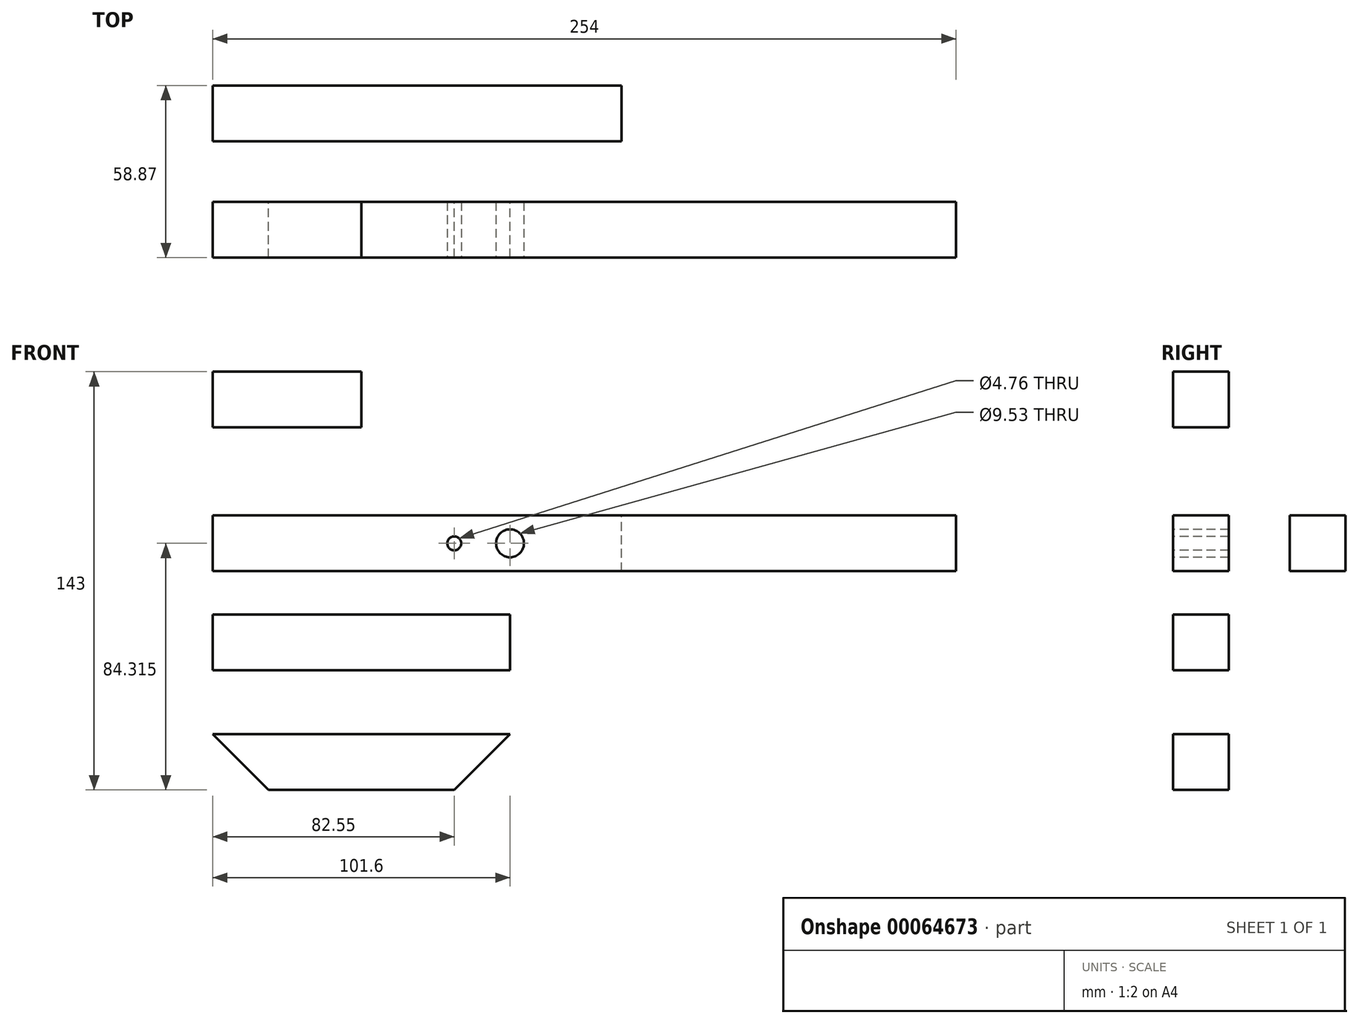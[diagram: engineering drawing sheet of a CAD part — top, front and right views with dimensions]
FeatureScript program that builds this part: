
annotation { "Feature Type Name" : "Feature", "Feature Type Description" : "" }
export const myFeature = defineFeature(function(context is Context, id is Id, definition is map)
    precondition{}
    {
        {
            var Q0;
            Q0=qCreatedBy(makeId("Front.planeOp"),FACE);
            var sketch = newSketch(context, id + "F0", { "sketchPlane" : qUnion([Q0])});
            skLineSegment(sketch, "E0.bottom", {"start": v(0, 0) * mm, "end": v(254, 0) * mm});
            skLineSegment(sketch, "E0.top", {"start": v(0, 19.05) * mm, "end": v(254, 19.05) * mm});
            skLineSegment(sketch, "E0.left", {"start": v(0, 0) * mm, "end": v(0, 19.05) * mm});
            skLineSegment(sketch, "E0.right", {"start": v(254, 0) * mm, "end": v(254, 19.05) * mm});
            skSolve(sketch);
        }
        {
            var Q0;
            Q0 = qSketchRegion(id + "F0", true);
            extrude(context, id + "F1", {"entities" : qUnion([Q0]), "depth" : 19.05 * mm});
        }
        {
            var Q0;
            Q0=makeQuery(id+"F1.opExtrude","CAP_FACE",FACE,{"disambiguationData":[OSD([sQuery(id+"F0.wireOp",EDGE,"E0.bottom"),sQuery(id+"F0.wireOp",EDGE,"E0.top"),sQuery(id+"F0.wireOp",EDGE,"E0.left"),sQuery(id+"F0.wireOp",EDGE,"E0.right")])],"isStart":false});
            var sketch = newSketch(context, id + "F2", { "sketchPlane" : qUnion([Q0])});
            skLineSegment(sketch, "E1", {"start": v(0, 9.53) * mm, "end": v(82.55, 9.53) * mm});
            skLineSegment(sketch, "E2", {"start": v(82.55, 9.53) * mm, "end": v(101.6, 9.53) * mm});
            skPoint(sketch, "E2.endSnap0", {"position": v(127, 19.05) * mm});
            skCircle(sketch, "E3", {"center": v(82.55, 9.53) * mm, "radius": 2.38 * mm});
            skCircle(sketch, "E4", {"center": v(101.6, 9.53) * mm, "radius": 4.76 * mm});
            skSolve(sketch);
        }
        {
            var Q0;
            Q0 = qSketchRegion(id + "F2", true);
            extrude(context, id + "F3", {"entities" : qUnion([Q0]), "operationType" : NewBodyOperationType.REMOVE, "oppositeDirection" : true, "depth" : 25.4 * mm});
        }
        {
            var Q0;
            Q0=qCreatedBy(makeId("Front.planeOp"),FACE);
            var sketch = newSketch(context, id + "F4", { "sketchPlane" : qUnion([Q0])});
            skLineSegment(sketch, "E5.bottom", {"start": v(0, -14.84) * mm, "end": v(101.6, -14.84) * mm});
            skLineSegment(sketch, "E5.top", {"start": v(0, -33.89) * mm, "end": v(101.6, -33.89) * mm});
            skLineSegment(sketch, "E5.left", {"start": v(0, -14.84) * mm, "end": v(0, -33.89) * mm});
            skLineSegment(sketch, "E5.right", {"start": v(101.6, -14.84) * mm, "end": v(101.6, -33.89) * mm});
            skSolve(sketch);
        }
        {
            var Q0;
            Q0 = qSketchRegion(id + "F4", true);
            extrude(context, id + "F5", {"entities" : qUnion([Q0]), "depth" : 19.05 * mm});
        }
        {
            var Q0;
            Q0=qCreatedBy(makeId("Front.planeOp"),FACE);
            var sketch = newSketch(context, id + "F6", { "sketchPlane" : qUnion([Q0])});
            skLineSegment(sketch, "E6.bottom", {"start": v(0, -55.74) * mm, "end": v(101.6, -55.74) * mm});
            skLineSegment(sketch, "E6.top", {"start": v(19.05, -74.8) * mm, "end": v(82.55, -74.8) * mm});
            skLineSegment(sketch, "E7", {"start": v(0, -55.74) * mm, "end": v(19.05, -74.8) * mm});
            skLineSegment(sketch, "E8", {"start": v(101.6, -55.74) * mm, "end": v(82.55, -74.8) * mm});
            skSolve(sketch);
        }
        {
            var Q0;
            Q0 = qSketchRegion(id + "F6", true);
            extrude(context, id + "F7", {"entities" : qUnion([Q0]), "depth" : 19.05 * mm});
        }
        {
            var Q0;
            Q0=qCreatedBy(makeId("Front.planeOp"),FACE);
            var sketch = newSketch(context, id + "F8", { "sketchPlane" : qUnion([Q0])});
            skLineSegment(sketch, "E9.bottom", {"start": v(0, 68.2) * mm, "end": v(50.8, 68.2) * mm});
            skLineSegment(sketch, "E9.top", {"start": v(0, 49.16) * mm, "end": v(50.8, 49.16) * mm});
            skLineSegment(sketch, "E9.left", {"start": v(0, 68.2) * mm, "end": v(0, 49.16) * mm});
            skLineSegment(sketch, "E9.right", {"start": v(50.8, 68.2) * mm, "end": v(50.8, 49.16) * mm});
            skSolve(sketch);
        }
        {
            var Q0;
            Q0 = qSketchRegion(id + "F8", true);
            extrude(context, id + "F9", {"entities" : qUnion([Q0]), "depth" : 19.05 * mm});
        }
        {
            var Q0;
            Q0=qCreatedBy(makeId("Right.planeOp"), FACE);
            var sketch = newSketch(context, id + "F10", { "sketchPlane" : qUnion([Q0])});
            skLineSegment(sketch, "E10.bottom", {"start": v(20.77, 0) * mm, "end": v(39.82, 0) * mm});
            skLineSegment(sketch, "E10.top", {"start": v(20.77, 19.05) * mm, "end": v(39.82, 19.05) * mm});
            skLineSegment(sketch, "E10.left", {"start": v(20.77, 0) * mm, "end": v(20.77, 19.05) * mm});
            skLineSegment(sketch, "E10.right", {"start": v(39.82, 0) * mm, "end": v(39.82, 19.05) * mm});
            skSolve(sketch);
        }
        {
            var Q0;
            Q0 = qSketchRegion(id + "F10", true);
            extrude(context, id + "F11", {"entities" : qUnion([Q0]), "depth" : 139.7 * mm, "offsetDistance" : 25.4 * mm});
        }
    });
